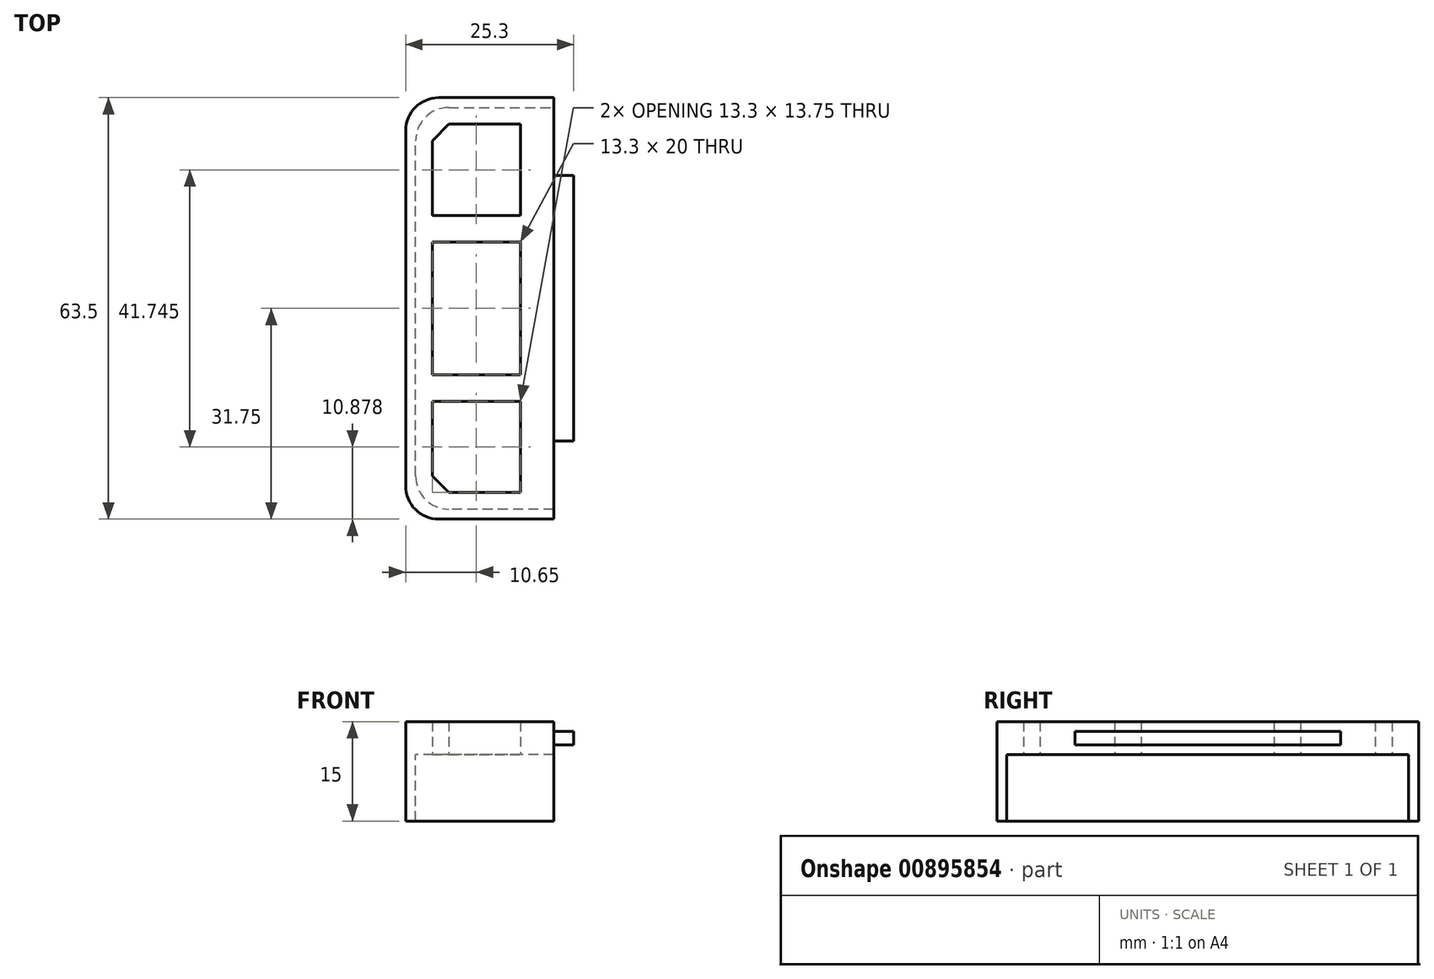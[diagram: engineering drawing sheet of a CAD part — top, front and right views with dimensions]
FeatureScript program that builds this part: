
annotation { "Feature Type Name" : "Feature", "Feature Type Description" : "" }
export const myFeature = defineFeature(function(context is Context, id is Id, definition is map)
    precondition{}
    {
        {
            var Q0;
            Q0=qCreatedBy(makeId("Right.planeOp"),FACE);
            var sketch = newSketch(context, id + "F0", { "sketchPlane" : qUnion([Q0])});
            skLineSegment(sketch, "E0.bottom", {"start": v(-31.75, 0) * mm, "end": v(31.75, 0) * mm});
            skLineSegment(sketch, "E0.top", {"start": v(-31.75, 5) * mm, "end": v(31.75, 5) * mm});
            skLineSegment(sketch, "E0.left", {"start": v(-31.75, 0) * mm, "end": v(-31.75, 5) * mm});
            skLineSegment(sketch, "E0.right", {"start": v(31.75, 0) * mm, "end": v(31.75, 5) * mm});
            skSolve(sketch);
        }
        {
            var Q0;
            Q0=makeQuery(id+"F0.imprint","IMPRINT",FACE,{"disambiguationData":[TD([[makeQuery(id+"F0.imprint","IMPRINT",EDGE,{"derivedFrom":sQuery(id+"F0.wireOp",EDGE,"E0.bottom")}),1.0]])]});
            extrude(context, id + "F1", {"entities" : qUnion([Q0]), "oppositeDirection" : true, "depth" : 22.3 * mm, "offsetDistance" : 25 * mm});
        }
        {
            var Q0;
            Q0=makeQuery(id+"F1.opExtrude","CAP_FACE",FACE,{"disambiguationData":[OSD([sQuery(id+"F0.wireOp",EDGE,"E0.bottom"),sQuery(id+"F0.wireOp",EDGE,"E0.top"),sQuery(id+"F0.wireOp",EDGE,"E0.left"),sQuery(id+"F0.wireOp",EDGE,"E0.right")])],"isStart":true});
            var sketch = newSketch(context, id + "F2", { "sketchPlane" : qUnion([Q0])});
            skLineSegment(sketch, "E1.bottom", {"start": v(-20, 1.5) * mm, "end": v(20, 1.5) * mm});
            skLineSegment(sketch, "E1.top", {"start": v(-20, 3.5) * mm, "end": v(20, 3.5) * mm});
            skLineSegment(sketch, "E1.left", {"start": v(-20, 1.5) * mm, "end": v(-20, 3.5) * mm});
            skLineSegment(sketch, "E1.right", {"start": v(20, 1.5) * mm, "end": v(20, 3.5) * mm});
            skPoint(sketch, "E1.middle", {"position": v(0, 2.5) * mm});
            skPoint(sketch, "E1.middle.positionSnap0", {"position": v(-31.75, 2.5) * mm});
            skPoint(sketch, "E1.middle.positionSnap1", {"position": v(0, 5) * mm});
            skPoint(sketch, "E1.centerSnap0", {"position": v(-31.75, 2.5) * mm});
            skPoint(sketch, "E1.centerSnap1", {"position": v(0, 5) * mm});
            skSolve(sketch);
        }
        {
            var Q0;
            Q0 = qSketchRegion(id + "F2", true);
            extrude(context, id + "F3", {"entities" : qUnion([Q0]), "operationType" : NewBodyOperationType.ADD, "depth" : 3 * mm, "offsetDistance" : 25 * mm});
        }
        {
            var Q0;
            Q0=makeQuery(id+"F1.opExtrude","SWEPT_FACE",FACE,{"disambiguationData":[OSD([sQuery(id+"F0.wireOp",EDGE,"E0.bottom")])]});
            var sketch = newSketch(context, id + "F4", { "sketchPlane" : qUnion([Q0])});
            skLineSegment(sketch, "E2", {"start": v(0, 31.75) * mm, "end": v(0, 30.25) * mm});
            skLineSegment(sketch, "E3", {"start": v(0, 30.25) * mm, "end": v(-20.8, 30.24) * mm});
            skLineSegment(sketch, "E4", {"start": v(-20.8, 30.24) * mm, "end": v(-20.8, -30.25) * mm});
            skLineSegment(sketch, "E5", {"start": v(-20.8, -30.25) * mm, "end": v(0, -30.25) * mm});
            skLineSegment(sketch, "E6", {"start": v(0, -30.25) * mm, "end": v(0, -31.75) * mm});
            skLineSegment(sketch, "E7", {"start": v(0, -31.75) * mm, "end": v(-22.3, -31.75) * mm});
            skLineSegment(sketch, "E8", {"start": v(-22.3, -31.75) * mm, "end": v(-22.3, 31.75) * mm});
            skLineSegment(sketch, "E9", {"start": v(-22.3, 31.75) * mm, "end": v(0, 31.75) * mm});
            skSolve(sketch);
        }
        {
            var Q0;
            Q0 = qSketchRegion(id + "F4", true);
            extrude(context, id + "F5", {"entities" : qUnion([Q0]), "operationType" : NewBodyOperationType.ADD, "depth" : 10 * mm, "offsetDistance" : 25 * mm});
        }
        {
            var Q0;
            Q0=makeQuery(id+"F5.boolean.opBoolean","MERGE",EDGE,{"derivedFrom":[makeQuery(id+"F1.opExtrude","CAP_EDGE",EDGE,{"disambiguationData":[OSD([sQuery(id+"F0.wireOp",EDGE,"E0.left")])],"isStart":false}),makeQuery(id+"F5.opExtrude","SWEPT_EDGE",EDGE,{"disambiguationData":[OSD([sQuery(id+"F4.wireOp",EDGE,"E8"),sQuery(id+"F4.wireOp",EDGE,"E9")])]})]});
            var Q1;
            Q1=makeQuery(id+"F5.boolean.opBoolean","MERGE",EDGE,{"derivedFrom":[makeQuery(id+"F1.opExtrude","CAP_EDGE",EDGE,{"disambiguationData":[OSD([sQuery(id+"F0.wireOp",EDGE,"E0.right")])],"isStart":false}),makeQuery(id+"F5.opExtrude","SWEPT_EDGE",EDGE,{"disambiguationData":[OSD([sQuery(id+"F4.wireOp",EDGE,"E7"),sQuery(id+"F4.wireOp",EDGE,"E8")])]})]});
            var Q2;
            Q2=makeQuery(id+"F5.opExtrude","SWEPT_EDGE",EDGE,{"disambiguationData":[OSD([sQuery(id+"F4.wireOp",EDGE,"E4"),sQuery(id+"F4.wireOp",EDGE,"E5")])]});
            var Q3;
            Q3=makeQuery(id+"F5.opExtrude","SWEPT_EDGE",EDGE,{"disambiguationData":[OSD([sQuery(id+"F4.wireOp",EDGE,"E3"),sQuery(id+"F4.wireOp",EDGE,"E4")])]});
            fillet(context, id + "F6", {"entities" : qUnion([Q0, Q1, Q2, Q3]), "radius" : 5 * mm, "tangentPropagation" : true, "allowEdgeOverflow" : false});
        }
        {
            var Q0;
            Q0=makeQuery(id+"F1.opExtrude","SWEPT_FACE",FACE,{"disambiguationData":[OSD([sQuery(id+"F0.wireOp",EDGE,"E0.bottom")])]});
            var sketch = newSketch(context, id + "F7", { "sketchPlane" : qUnion([Q0])});
            skLineSegment(sketch, "E10.bottom", {"start": v(-18.3, 10) * mm, "end": v(-5, 10) * mm});
            skLineSegment(sketch, "E10.top", {"start": v(-18.3, -10) * mm, "end": v(-5, -10) * mm});
            skLineSegment(sketch, "E10.left", {"start": v(-18.3, 10) * mm, "end": v(-18.3, -10) * mm});
            skLineSegment(sketch, "E10.right", {"start": v(-5, 10) * mm, "end": v(-5, -10) * mm});
            skPoint(sketch, "E10.middle", {"position": v(-11.65, 0) * mm});
            skLineSegment(sketch, "E11", {"start": v(-5, 14) * mm, "end": v(-5, 27.75) * mm});
            skLineSegment(sketch, "E12", {"start": v(-5, 27.75) * mm, "end": v(-15.8, 27.75) * mm});
            skLineSegment(sketch, "E13", {"start": v(-15.8, 27.75) * mm, "end": v(-18.3, 25.24) * mm});
            skLineSegment(sketch, "E14", {"start": v(-18.3, 25.25) * mm, "end": v(-18.3, 14) * mm});
            skLineSegment(sketch, "E15", {"start": v(-18.3, 14) * mm, "end": v(-5, 14) * mm});
            skLineSegment(sketch, "E16", {"start": v(-5, -14) * mm, "end": v(-18.3, -14) * mm});
            skLineSegment(sketch, "E17", {"start": v(-18.3, -14) * mm, "end": v(-18.3, -25.25) * mm});
            skLineSegment(sketch, "E18", {"start": v(-18.3, -25.25) * mm, "end": v(-15.8, -27.75) * mm});
            skLineSegment(sketch, "E19", {"start": v(-15.8, -27.75) * mm, "end": v(-5, -27.75) * mm});
            skLineSegment(sketch, "E20", {"start": v(-5, -27.75) * mm, "end": v(-5, -14) * mm});
            skSolve(sketch);
        }
        {
            var Q0;
            Q0 = qSketchRegion(id + "F7", true);
            extrude(context, id + "F8", {"entities" : qUnion([Q0]), "operationType" : NewBodyOperationType.REMOVE, "oppositeDirection" : true, "depth" : 25 * mm, "offsetDistance" : 25 * mm});
        }
    });
